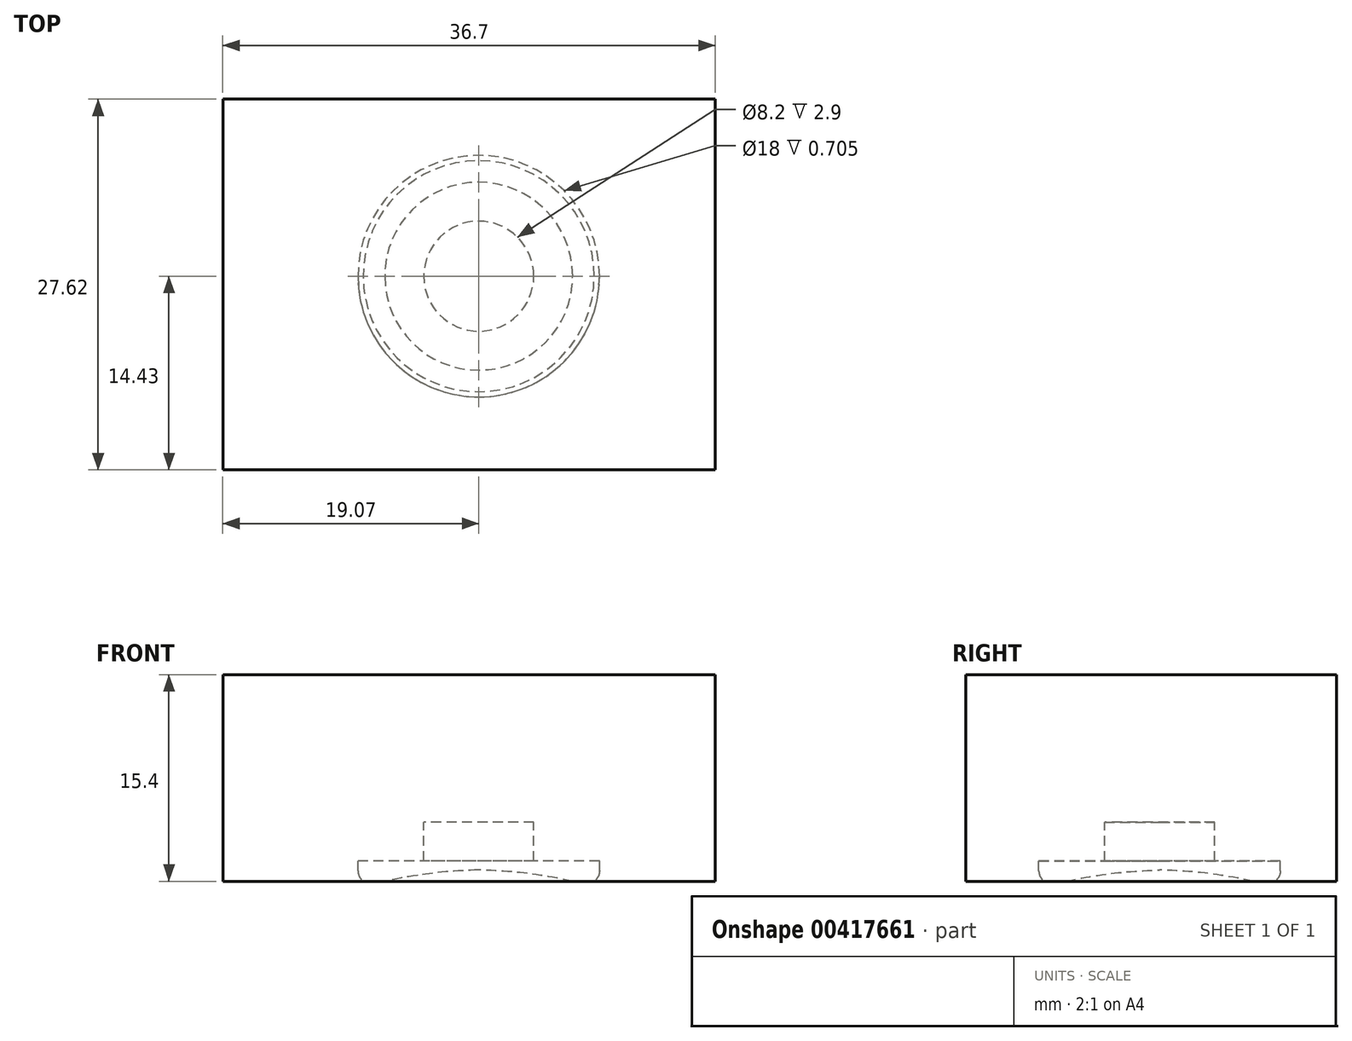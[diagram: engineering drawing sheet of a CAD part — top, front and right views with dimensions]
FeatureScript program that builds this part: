
annotation { "Feature Type Name" : "Feature", "Feature Type Description" : "" }
export const myFeature = defineFeature(function(context is Context, id is Id, definition is map)
    precondition{}
    {
        {
            var Q0;
            Q0=qCreatedBy(makeId("Front.planeOp"),FACE);
            var sketch = newSketch(context, id + "F0", { "sketchPlane" : qUnion([Q0])});
            skLineSegment(sketch, "E0", {"start": v(9, 0) * mm, "end": v(9, 2) * mm});
            skLineSegment(sketch, "E1", {"start": v(9, 2) * mm, "end": v(4.1, 2) * mm});
            skLineSegment(sketch, "E2", {"start": v(4.1, 2) * mm, "end": v(4.1, 4.9) * mm});
            skPoint(sketch, "E3.orphan", {"position": v(4.1, 0) * mm});
            skLineSegment(sketch, "E4", {"start": v(4.1, 4.9) * mm, "end": v(0, 4.9) * mm});
            skLineSegment(sketch, "E5", {"start": v(0, 4.9) * mm, "end": v(0, 1.34) * mm});
            skArc(sketch, "E6", {"start": v(9, 0) * mm, "mid": v(4.54, 0.95) * mm, "end": v(0, 1.34) * mm});
            skSolve(sketch);
        }
        {
            var Q0;
            Q0=makeQuery(id+"F0.imprint","IMPRINT",FACE,{"disambiguationData":[TD([[makeQuery(id+"F0.imprint","IMPRINT",EDGE,{"derivedFrom":sQuery(id+"F0.wireOp",EDGE,"E0")}),1.0]])]});
            var Q1;
            Q1=sQuery(id+"F0.wireOp",EDGE,"E5");
            revolve(context, id + "F1", {"entities" : qUnion([Q0]), "axis" : qUnion([Q1]), "revolveType" : RevolveType.FULL});
        }
        {
            var Q0;
            Q0=makeQuery(id+"F1.opRevolve","SWEPT_EDGE",EDGE,{"disambiguationData":[OSD([sQuery(id+"F0.wireOp",EDGE,"E0"),sQuery(id+"F0.wireOp",EDGE,"E6")])]});
            fillet(context, id + "F2", {"entities" : qUnion([Q0]), "radius" : 1 * mm, "tangentPropagation" : true, "allowEdgeOverflow" : false});
        }
        {
            var Q0;
            Q0=qCreatedBy(makeId("Top.planeOp"),FACE);
            cPlane(context, id + "F3", {"entities" : qUnion([Q0]), "cplaneType" : CPlaneType.OFFSET, "offset" : .5 * mm, "width" : 150 * mm, "height" : 150 * mm});
        }
        {
            var Q0;
            Q0=qCreatedBy(id+"F3.planeOp",FACE);
            var sketch = newSketch(context, id + "F4", { "sketchPlane" : qUnion([Q0])});
            skLineSegment(sketch, "E7.bottom", {"start": v(-19.07, 13.2) * mm, "end": v(17.63, 13.2) * mm});
            skLineSegment(sketch, "E7.top", {"start": v(-19.07, -14.43) * mm, "end": v(17.63, -14.43) * mm});
            skLineSegment(sketch, "E7.left", {"start": v(-19.07, 13.2) * mm, "end": v(-19.07, -14.43) * mm});
            skLineSegment(sketch, "E7.right", {"start": v(17.63, 13.2) * mm, "end": v(17.63, -14.43) * mm});
            skSolve(sketch);
        }
        {
            var Q0;
            Q0=makeQuery(id+"F4.imprint","IMPRINT",FACE,{"disambiguationData":[TD([[makeQuery(id+"F4.imprint","IMPRINT",EDGE,{"derivedFrom":sQuery(id+"F4.wireOp",EDGE,"E7.bottom")}),-1.0]])]});
            extrude(context, id + "F5", {"entities" : qUnion([Q0]), "depth" : 15.4 * mm});
        }
        {
            var Q0;
            Q0=makeQuery(id+"F1.opRevolve","SWEPT_BODY",BODY,{"disambiguationData":[OSD([sQuery(id+"F0.wireOp",EDGE,"E0"),sQuery(id+"F0.wireOp",EDGE,"E1"),sQuery(id+"F0.wireOp",EDGE,"E2"),sQuery(id+"F0.wireOp",EDGE,"E4"),sQuery(id+"F0.wireOp",EDGE,"E5"),sQuery(id+"F0.wireOp",EDGE,"E6")])]});
            var Q1;
            Q1=makeQuery(id+"F5.opExtrude","SWEPT_BODY",BODY,{"disambiguationData":[OSD([sQuery(id+"F4.wireOp",EDGE,"E7.bottom"),sQuery(id+"F4.wireOp",EDGE,"E7.top"),sQuery(id+"F4.wireOp",EDGE,"E7.left"),sQuery(id+"F4.wireOp",EDGE,"E7.right")])]});
            booleanBodies(context, id + "F6", {"operationType" : BooleanOperationType.SUBTRACTION, "tools" : qUnion([Q0]), "targets" : qUnion([Q1])});
        }
    });
